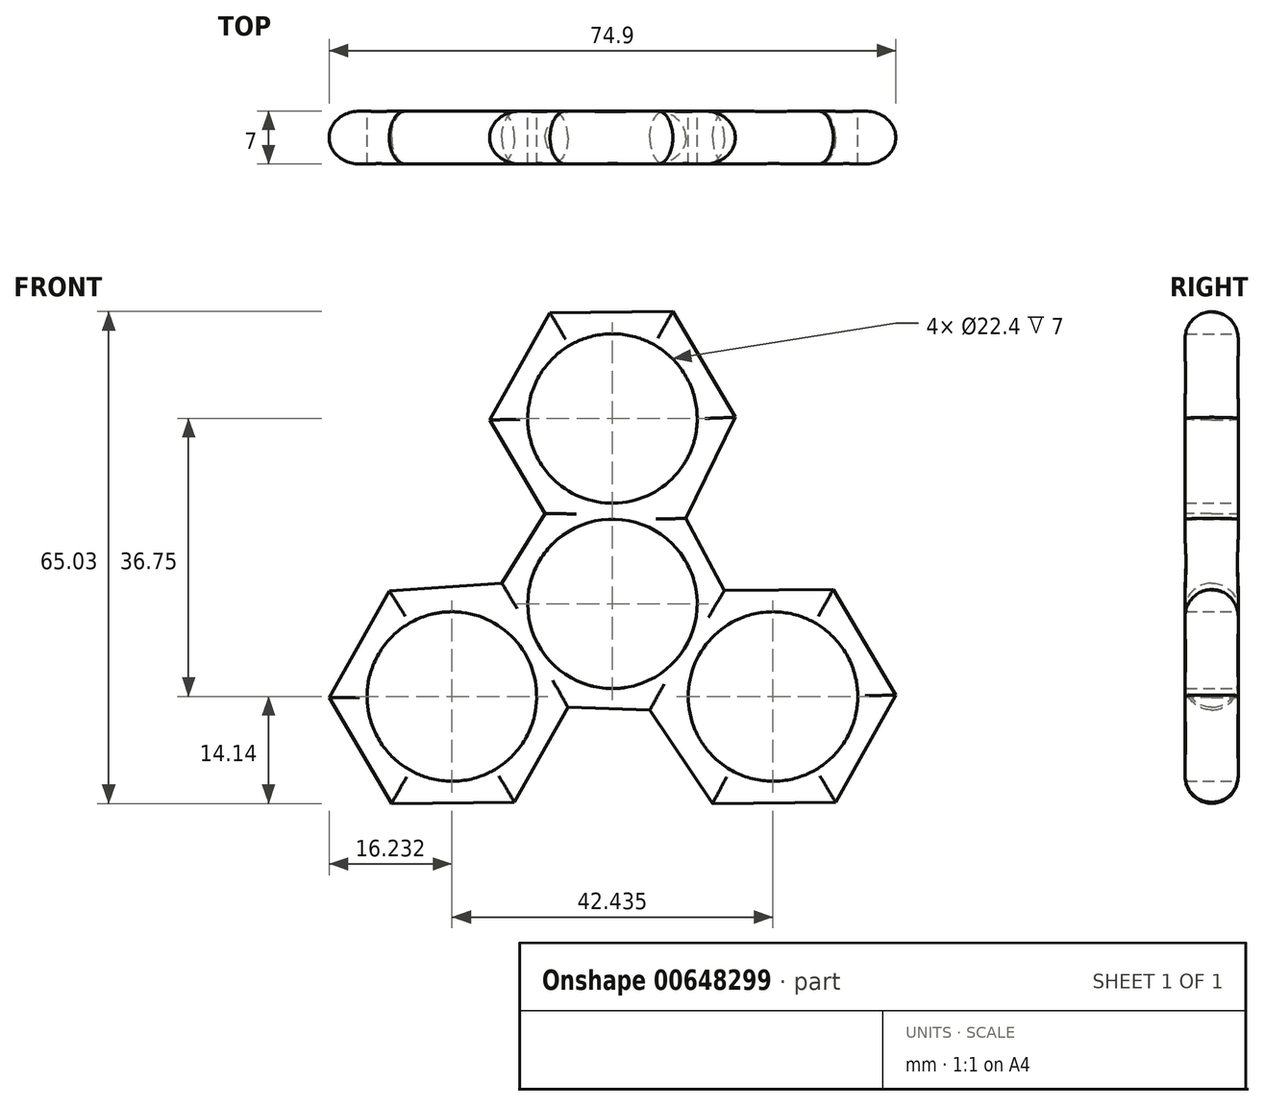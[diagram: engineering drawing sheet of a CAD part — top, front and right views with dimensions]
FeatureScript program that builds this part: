
annotation { "Feature Type Name" : "Feature", "Feature Type Description" : "" }
export const myFeature = defineFeature(function(context is Context, id is Id, definition is map)
    precondition{}
    {
        {
            var Q0;
            Q0=qCreatedBy(makeId("Front.planeOp"),FACE);
            var sketch = newSketch(context, id + "F0", { "sketchPlane" : qUnion([Q0])});
            skCircle(sketch, "E0", {"center": v(0, 0) * mm, "radius": 11.2 * mm});
            skCircle(sketch, "E1", {"center": v(0, 24.5) * mm, "radius": 11.2 * mm});
            skCircle(sketch, "E2.1.0", {"center": v(-21.22, -12.25) * mm, "radius": 11.2 * mm});
            skCircle(sketch, "E2.2.0", {"center": v(21.22, -12.25) * mm, "radius": 11.2 * mm});
            skLineSegment(sketch, "E3.0", {"start": v(-5.88, -13.68) * mm, "end": v(-12.96, -26.22) * mm});
            skLineSegment(sketch, "E3.1", {"start": v(-12.96, -26.22) * mm, "end": v(-29.19, -26.39) * mm});
            skLineSegment(sketch, "E3.2", {"start": v(-29.19, -26.39) * mm, "end": v(-37.45, -12.42) * mm});
            skLineSegment(sketch, "E3.3", {"start": v(-37.45, -12.42) * mm, "end": v(-29.48, 1.72) * mm});
            skLineSegment(sketch, "E3.4", {"start": v(-29.48, 1.72) * mm, "end": v(-14.62, 2.75) * mm});
            skPoint(sketch, "E3.0.midPoint", {"position": v(-9.42, -19.95) * mm});
            skLineSegment(sketch, "E4.1.0", {"start": v(13.25, -26.39) * mm, "end": v(4.93, -14.04) * mm});
            skLineSegment(sketch, "E4.2.0", {"start": v(16.23, 24.67) * mm, "end": v(9.7, 11.3) * mm});
            skLineSegment(sketch, "E5.1.0", {"start": v(29.48, -26.22) * mm, "end": v(13.25, -26.39) * mm});
            skLineSegment(sketch, "E5.2.0", {"start": v(7.97, 38.64) * mm, "end": v(16.23, 24.67) * mm});
            skLineSegment(sketch, "E6.1.0", {"start": v(37.45, -12.08) * mm, "end": v(29.48, -26.22) * mm});
            skLineSegment(sketch, "E6.2.0", {"start": v(-8.26, 38.47) * mm, "end": v(7.97, 38.64) * mm});
            skLineSegment(sketch, "E7.1.0", {"start": v(29.19, 1.89) * mm, "end": v(37.45, -12.08) * mm});
            skLineSegment(sketch, "E7.2.0", {"start": v(-16.23, 24.33) * mm, "end": v(-8.26, 38.47) * mm});
            skLineSegment(sketch, "E8.1.0", {"start": v(14.79, 1.74) * mm, "end": v(29.19, 1.89) * mm});
            skLineSegment(sketch, "E8.2.0", {"start": v(-8.9, 11.93) * mm, "end": v(-16.23, 24.33) * mm});
            skLineSegment(sketch, "E9", {"start": v(-14.62, 2.75) * mm, "end": v(-8.9, 11.93) * mm});
            skLineSegment(sketch, "E10", {"start": v(9.7, 11.3) * mm, "end": v(14.79, 1.74) * mm});
            skLineSegment(sketch, "E11", {"start": v(4.93, -14.04) * mm, "end": v(-5.88, -13.68) * mm});
            skPoint(sketch, "E12.orphan", {"position": v(12.96, 1.72) * mm});
            skSolve(sketch);
        }
        {
            var Q0;
            Q0=makeQuery(id+"F0.imprint","IMPRINT",FACE,{"disambiguationData":[TD([[makeQuery(id+"F0.imprint","IMPRINT",EDGE,{"derivedFrom":sQuery(id+"F0.wireOp",EDGE,"E0")}),-1.0]])]});
            extrude(context, id + "F1", {"entities" : qUnion([Q0]), "depth" : 7 * mm, "offsetDistance" : 25.4 * mm});
        }
        {
            var Q0;
            Q0=makeQuery(id+"F1.opExtrude","CAP_EDGE",EDGE,{"disambiguationData":[OSD([sQuery(id+"F0.wireOp",EDGE,"E6.2.0")])],"isStart":false});
            var Q1;
            Q1=makeQuery(id+"F1.opExtrude","CAP_EDGE",EDGE,{"disambiguationData":[OSD([sQuery(id+"F0.wireOp",EDGE,"E5.2.0")])],"isStart":false});
            var Q2;
            Q2=makeQuery(id+"F1.opExtrude","CAP_EDGE",EDGE,{"disambiguationData":[OSD([sQuery(id+"F0.wireOp",EDGE,"E4.2.0")])],"isStart":false});
            var Q3;
            Q3=makeQuery(id+"F1.opExtrude","CAP_EDGE",EDGE,{"disambiguationData":[OSD([sQuery(id+"F0.wireOp",EDGE,"E10")])],"isStart":false});
            var Q4;
            Q4=makeQuery(id+"F1.opExtrude","CAP_EDGE",EDGE,{"disambiguationData":[OSD([sQuery(id+"F0.wireOp",EDGE,"E8.1.0")])],"isStart":false});
            var Q5;
            Q5=makeQuery(id+"F1.opExtrude","CAP_EDGE",EDGE,{"disambiguationData":[OSD([sQuery(id+"F0.wireOp",EDGE,"E7.1.0")])],"isStart":false});
            var Q6;
            Q6=makeQuery(id+"F1.opExtrude","CAP_EDGE",EDGE,{"disambiguationData":[OSD([sQuery(id+"F0.wireOp",EDGE,"E6.1.0")])],"isStart":false});
            var Q7;
            Q7=makeQuery(id+"F1.opExtrude","CAP_EDGE",EDGE,{"disambiguationData":[OSD([sQuery(id+"F0.wireOp",EDGE,"E5.1.0")])],"isStart":false});
            var Q8;
            Q8=makeQuery(id+"F1.opExtrude","CAP_EDGE",EDGE,{"disambiguationData":[OSD([sQuery(id+"F0.wireOp",EDGE,"E4.1.0")])],"isStart":false});
            var Q9;
            Q9=makeQuery(id+"F1.opExtrude","CAP_EDGE",EDGE,{"disambiguationData":[OSD([sQuery(id+"F0.wireOp",EDGE,"E11")])],"isStart":false});
            var Q10;
            Q10=makeQuery(id+"F1.opExtrude","CAP_EDGE",EDGE,{"disambiguationData":[OSD([sQuery(id+"F0.wireOp",EDGE,"E3.0")])],"isStart":false});
            var Q11;
            Q11=makeQuery(id+"F1.opExtrude","CAP_EDGE",EDGE,{"disambiguationData":[OSD([sQuery(id+"F0.wireOp",EDGE,"E3.1")])],"isStart":false});
            var Q12;
            Q12=makeQuery(id+"F1.opExtrude","CAP_EDGE",EDGE,{"disambiguationData":[OSD([sQuery(id+"F0.wireOp",EDGE,"E3.2")])],"isStart":false});
            var Q13;
            Q13=makeQuery(id+"F1.opExtrude","CAP_EDGE",EDGE,{"disambiguationData":[OSD([sQuery(id+"F0.wireOp",EDGE,"E3.3")])],"isStart":false});
            var Q14;
            Q14=makeQuery(id+"F1.opExtrude","CAP_EDGE",EDGE,{"disambiguationData":[OSD([sQuery(id+"F0.wireOp",EDGE,"E3.4")])],"isStart":false});
            var Q15;
            Q15=makeQuery(id+"F1.opExtrude","CAP_EDGE",EDGE,{"disambiguationData":[OSD([sQuery(id+"F0.wireOp",EDGE,"E9")])],"isStart":false});
            var Q16;
            Q16=makeQuery(id+"F1.opExtrude","CAP_EDGE",EDGE,{"disambiguationData":[OSD([sQuery(id+"F0.wireOp",EDGE,"E8.2.0")])],"isStart":false});
            var Q17;
            Q17=makeQuery(id+"F1.opExtrude","CAP_EDGE",EDGE,{"disambiguationData":[OSD([sQuery(id+"F0.wireOp",EDGE,"E7.2.0")])],"isStart":false});
            fillet(context, id + "F2", {"entities" : qUnion([Q0, Q1, Q2, Q3, Q4, Q5, Q6, Q7, Q8, Q9, Q10, Q11, Q12, Q13, Q14, Q15, Q16, Q17]), "radius" : 3.5 * mm, "tangentPropagation" : true, "allowEdgeOverflow" : false});
        }
        {
            var Q0;
            Q0=makeQuery(id+"F1.opExtrude","CAP_EDGE",EDGE,{"disambiguationData":[OSD([sQuery(id+"F0.wireOp",EDGE,"E6.2.0")])],"isStart":true});
            var Q1;
            Q1=makeQuery(id+"F1.opExtrude","CAP_EDGE",EDGE,{"disambiguationData":[OSD([sQuery(id+"F0.wireOp",EDGE,"E7.2.0")])],"isStart":true});
            var Q2;
            Q2=makeQuery(id+"F1.opExtrude","CAP_EDGE",EDGE,{"disambiguationData":[OSD([sQuery(id+"F0.wireOp",EDGE,"E5.2.0")])],"isStart":true});
            var Q3;
            Q3=makeQuery(id+"F1.opExtrude","CAP_EDGE",EDGE,{"disambiguationData":[OSD([sQuery(id+"F0.wireOp",EDGE,"E4.2.0")])],"isStart":true});
            var Q4;
            Q4=makeQuery(id+"F1.opExtrude","CAP_EDGE",EDGE,{"disambiguationData":[OSD([sQuery(id+"F0.wireOp",EDGE,"E10")])],"isStart":true});
            var Q5;
            Q5=makeQuery(id+"F1.opExtrude","CAP_EDGE",EDGE,{"disambiguationData":[OSD([sQuery(id+"F0.wireOp",EDGE,"E8.1.0")])],"isStart":true});
            var Q6;
            Q6=makeQuery(id+"F1.opExtrude","CAP_EDGE",EDGE,{"disambiguationData":[OSD([sQuery(id+"F0.wireOp",EDGE,"E7.1.0")])],"isStart":true});
            var Q7;
            Q7=makeQuery(id+"F1.opExtrude","CAP_EDGE",EDGE,{"disambiguationData":[OSD([sQuery(id+"F0.wireOp",EDGE,"E6.1.0")])],"isStart":true});
            var Q8;
            Q8=makeQuery(id+"F1.opExtrude","CAP_EDGE",EDGE,{"disambiguationData":[OSD([sQuery(id+"F0.wireOp",EDGE,"E5.1.0")])],"isStart":true});
            var Q9;
            Q9=makeQuery(id+"F1.opExtrude","CAP_EDGE",EDGE,{"disambiguationData":[OSD([sQuery(id+"F0.wireOp",EDGE,"E4.1.0")])],"isStart":true});
            var Q10;
            Q10=makeQuery(id+"F1.opExtrude","CAP_EDGE",EDGE,{"disambiguationData":[OSD([sQuery(id+"F0.wireOp",EDGE,"E11")])],"isStart":true});
            var Q11;
            Q11=makeQuery(id+"F1.opExtrude","CAP_EDGE",EDGE,{"disambiguationData":[OSD([sQuery(id+"F0.wireOp",EDGE,"E3.0")])],"isStart":true});
            var Q12;
            Q12=makeQuery(id+"F1.opExtrude","CAP_EDGE",EDGE,{"disambiguationData":[OSD([sQuery(id+"F0.wireOp",EDGE,"E3.1")])],"isStart":true});
            var Q13;
            Q13=makeQuery(id+"F1.opExtrude","CAP_EDGE",EDGE,{"disambiguationData":[OSD([sQuery(id+"F0.wireOp",EDGE,"E3.2")])],"isStart":true});
            var Q14;
            Q14=makeQuery(id+"F1.opExtrude","CAP_EDGE",EDGE,{"disambiguationData":[OSD([sQuery(id+"F0.wireOp",EDGE,"E3.3")])],"isStart":true});
            var Q15;
            Q15=makeQuery(id+"F1.opExtrude","CAP_EDGE",EDGE,{"disambiguationData":[OSD([sQuery(id+"F0.wireOp",EDGE,"E3.4")])],"isStart":true});
            var Q16;
            Q16=makeQuery(id+"F1.opExtrude","CAP_EDGE",EDGE,{"disambiguationData":[OSD([sQuery(id+"F0.wireOp",EDGE,"E9")])],"isStart":true});
            var Q17;
            Q17=makeQuery(id+"F1.opExtrude","CAP_EDGE",EDGE,{"disambiguationData":[OSD([sQuery(id+"F0.wireOp",EDGE,"E8.2.0")])],"isStart":true});
            fillet(context, id + "F3", {"entities" : qUnion([Q0, Q1, Q2, Q3, Q4, Q5, Q6, Q7, Q8, Q9, Q10, Q11, Q12, Q13, Q14, Q15, Q16, Q17]), "radius" : 3.5 * mm, "tangentPropagation" : true, "allowEdgeOverflow" : false});
        }
    });
